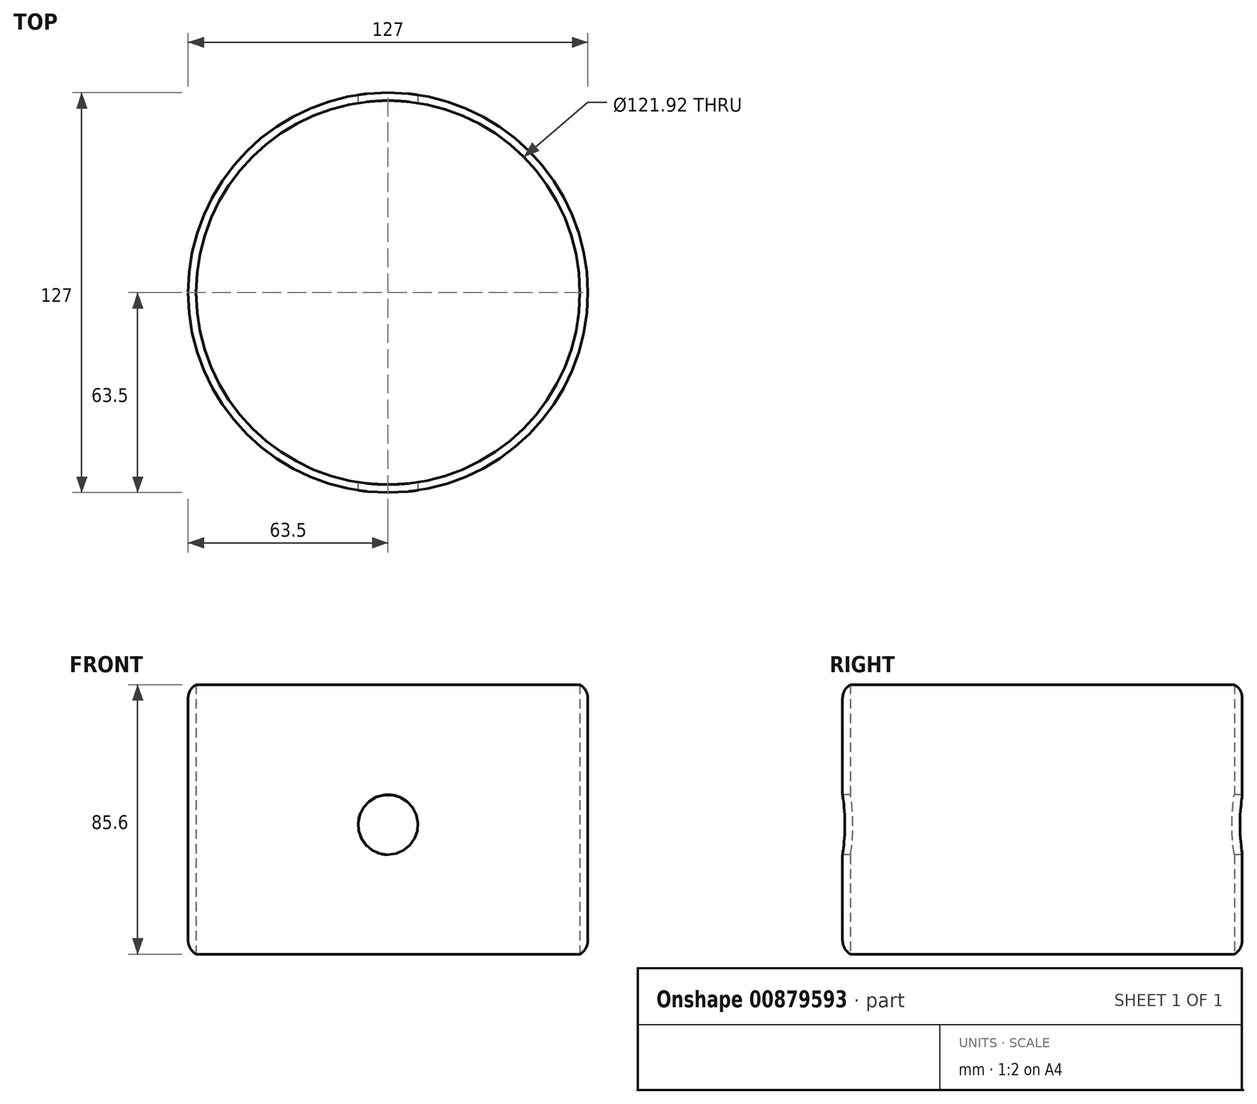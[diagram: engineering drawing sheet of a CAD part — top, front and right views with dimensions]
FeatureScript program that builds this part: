
annotation { "Feature Type Name" : "Feature", "Feature Type Description" : "" }
export const myFeature = defineFeature(function(context is Context, id is Id, definition is map)
    precondition{}
    {
        {
            var Q0;
            Q0=qCreatedBy(makeId("Top.planeOp"),FACE);
            var sketch = newSketch(context, id + "F0", { "sketchPlane" : qUnion([Q0])});
            skCircle(sketch, "E0", {"center": v(0, 0) * mm, "radius": 63.5 * mm});
            skSolve(sketch);
        }
        {
            var Q0;
            Q0=makeQuery(id+"F0.imprint","IMPRINT",FACE,{"disambiguationData":[TD([[makeQuery(id+"F0.imprint","IMPRINT",EDGE,{"derivedFrom":sQuery(id+"F0.wireOp",EDGE,"E0")}),1.0]])]});
            extrude(context, id + "F1", {"entities" : qUnion([Q0]), "depth" : 85.6 * mm, "offsetDistance" : 25.4 * mm});
        }
        {
            var Q0;
            Q0=makeQuery(id+"F1.opExtrude","CAP_FACE",FACE,{"disambiguationData":[OSD([sQuery(id+"F0.wireOp",EDGE,"E0")])],"isStart":false});
            var Q1;
            Q1=makeQuery(id+"F1.opExtrude","CAP_FACE",FACE,{"disambiguationData":[OSD([sQuery(id+"F0.wireOp",EDGE,"E0")])],"isStart":true});
            shell(context, id + "F2", {"entities" : qUnion([Q0, Q1]), "thickness" : 2.54 * mm});
        }
        {
            var Q0;
            Q0=qCreatedBy(makeId("Front.planeOp"),FACE);
            var sketch = newSketch(context, id + "F3", { "sketchPlane" : qUnion([Q0])});
            skCircle(sketch, "E1", {"center": v(0, 41.1) * mm, "radius": 9.52 * mm});
            skSolve(sketch);
        }
        {
            var Q0;
            Q0=makeQuery(id+"F3.imprint","IMPRINT",FACE,{"disambiguationData":[TD([[makeQuery(id+"F3.imprint","IMPRINT",EDGE,{"derivedFrom":sQuery(id+"F3.wireOp",EDGE,"E1")}),1.0]])]});
            extrude(context, id + "F4", {"entities" : qUnion([Q0]), "operationType" : NewBodyOperationType.REMOVE, "oppositeDirection" : true, "depth" : 185.93 * mm, "offsetDistance" : 25.4 * mm, "symmetric" : true});
        }
        {
            var Q0;
            Q0=makeQuery(id+"F1.opExtrude","CAP_EDGE",EDGE,{"disambiguationData":[OSD([sQuery(id+"F0.wireOp",EDGE,"E0")])],"isStart":false});
            var Q1;
            Q1=makeQuery(id+"F1.opExtrude","CAP_EDGE",EDGE,{"disambiguationData":[OSD([sQuery(id+"F0.wireOp",EDGE,"E0")])],"isStart":true});
            fillet(context, id + "F5", {"entities" : qUnion([Q0, Q1]), "radius" : 5.08 * mm, "tangentPropagation" : true, "allowEdgeOverflow" : false});
        }
    });
